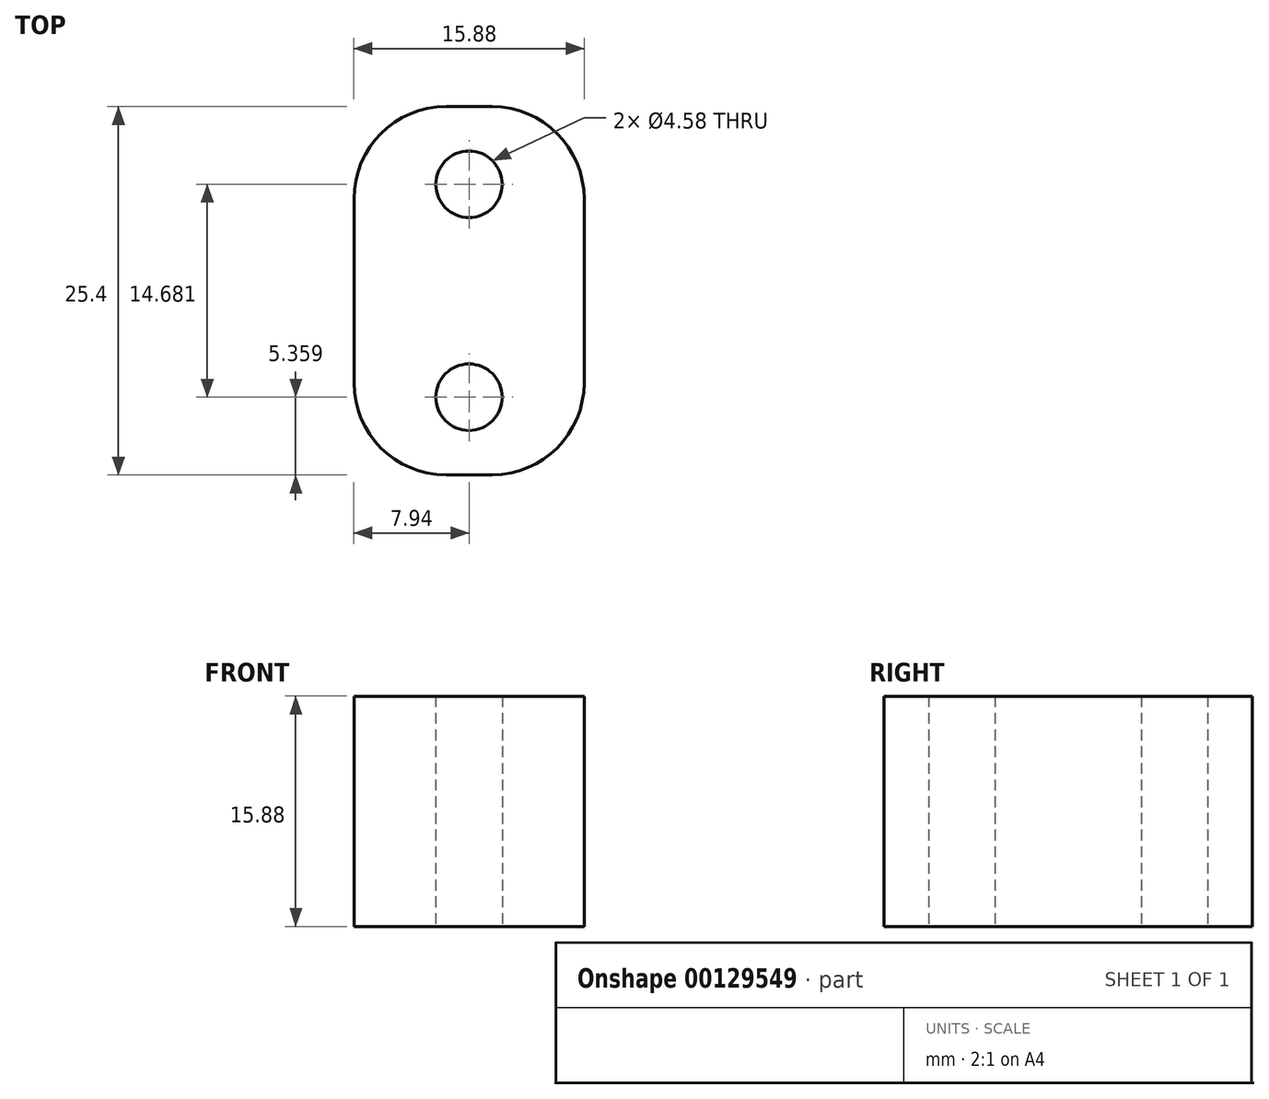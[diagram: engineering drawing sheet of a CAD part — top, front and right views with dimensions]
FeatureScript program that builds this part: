
annotation { "Feature Type Name" : "Feature", "Feature Type Description" : "" }
export const myFeature = defineFeature(function(context is Context, id is Id, definition is map)
    precondition{}
    {
        {
            var Q0;
            Q0=qCreatedBy(makeId("Top.planeOp"),FACE);
            var sketch = newSketch(context, id + "F0", { "sketchPlane" : qUnion([Q0])});
            skLineSegment(sketch, "E0", {"start": v(0, 23.66) * mm, "end": v(0, -17.61) * mm, "construction": true});
            skCircle(sketch, "E1", {"center": v(0, 7.34) * mm, "radius": 2.3 * mm});
            skCircle(sketch, "E2", {"center": v(0, -7.34) * mm, "radius": 2.3 * mm});
            skLineSegment(sketch, "E3", {"start": v(0, 7.34) * mm, "end": v(0, -7.34) * mm});
            skPoint(sketch, "E4", {"position": v(0, 0) * mm});
            skLineSegment(sketch, "E5.bottom", {"start": v(-1.59, 12.7) * mm, "end": v(1.59, 12.7) * mm});
            skLineSegment(sketch, "E5.top", {"start": v(-1.59, -12.7) * mm, "end": v(1.59, -12.7) * mm});
            skLineSegment(sketch, "E5.left", {"start": v(-7.94, 6.35) * mm, "end": v(-7.94, -6.35) * mm});
            skLineSegment(sketch, "E5.right", {"start": v(7.94, 6.35) * mm, "end": v(7.94, -6.35) * mm});
            skPoint(sketch, "E6.visualSharp", {"position": v(-7.94, 12.7) * mm});
            skArc(sketch, "E6.filletArc", {"start": v(-1.59, 12.7) * mm, "mid": v(-6.08, 10.84) * mm, "end": v(-7.94, 6.35) * mm});
            skPoint(sketch, "E7.visualSharp", {"position": v(7.94, 12.7) * mm});
            skArc(sketch, "E7.filletArc", {"start": v(7.94, 6.35) * mm, "mid": v(6.08, 10.84) * mm, "end": v(1.59, 12.7) * mm});
            skPoint(sketch, "E8.visualSharp", {"position": v(7.94, -12.7) * mm});
            skArc(sketch, "E8.filletArc", {"start": v(1.59, -12.7) * mm, "mid": v(6.08, -10.84) * mm, "end": v(7.94, -6.35) * mm});
            skPoint(sketch, "E9.visualSharp", {"position": v(-7.94, -12.7) * mm});
            skArc(sketch, "E9.filletArc", {"start": v(-7.94, -6.35) * mm, "mid": v(-6.08, -10.84) * mm, "end": v(-1.59, -12.7) * mm});
            skSolve(sketch);
        }
        {
            var Q0;
            Q0 = qSketchRegion(id + "F0", true);
            extrude(context, id + "F1", {"entities" : qUnion([Q0]), "depth" : 15.88 * mm});
        }
    });
